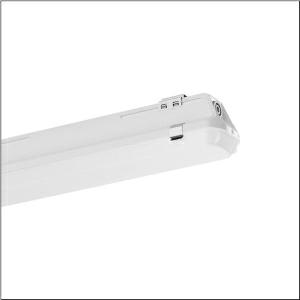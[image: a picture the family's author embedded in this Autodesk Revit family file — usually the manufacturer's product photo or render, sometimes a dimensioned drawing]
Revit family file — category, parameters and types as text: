
# Revit family: monsun_r__11_emergency_51fp107p437h3g_44d6
name_source: partatom
category: Lighting Fixtures
units: mm (PartAtom-declared; Revit-internal decimal feet)

## family parameters
Cut with Voids When Loaded = No
Host = Face
Light Source = No
Part Type = Normal
Room Calculation Point = No
Round Connector Dimension = Use Diameter
Shared = No

## types (1)
- Monsun® 11 emergency (1 x LED, 3840 lm, 24.5 W, 4000K)
    Apparent Load = 25 VA
    CIE Flux Codes = 47 77 93 94 100
    Color Rendering = 80
    Color Temperature = 4000K
    Default Elevation = 1800 mm
    Description = Monsun® 11 emergency, damp-proof luminaire, chain hanger, primary optical cover: enclosure, of PMMA, light emission: direct distribution, primary light characteristic: symmetric, installation type: suspended mounting, surface-mounted, horizontal mounting, vertical mounting, LED, rated luminous flux: 3.840lm, luminous efficacy: 157lm/W, light colour: 840, colour temperature: 4000K, control gear: ECG, with terminal, 4-pole, max. 2.5mm², mains connection: 220..240V, AC, 50/60Hz, rated input power: 25W, control gear: single battery element, battery: NiCd, 4,5Ah, mains connection: 230V, 50Hz, luminaire housing, of glass-fibre reinforced polyester, uncoated, bright grey, incl. chain hanger, length: 1.590mm, width: 90mm, height: 88mm, clip for enclosure, of stainless steel (V2A), ceiling mounting element, of stainless steel (V2A), chain hanger, of stainless steel (V2A), protection rating (complete): IP66, insulation class (complete): insulation class I (protective earthing), certification: CE, UKCA, protection symbol: D, impact resistance: IK04, permissible operating ambient temperature: +5..+35°C, standard: EN 50419, EN 60598-2-1, EN 60598-2-22, no direct snow, no direct sun, no direct rain, for indoor or canopied outdoor use, corresponds to IFS (International Featured Standards) requirements for safety and quality in the food industry, contact your sales advisor before using the luminaires in applications with unclear chemical exposure, large temperature fluctuations or condensation-forming humidity, LABS conformity tested according to VDMA 24364:2018-05, packaging unit: 1 piece
    Height = 89 mm
    Lamp = 1 x LED
    Lamp Light Flux = 3840 lm
    Lamp Power = 24.5 W
    Lamp count = 1
    Length = 1590 mm
    Luminous efficacy = 157 lm/W
    Manufacturer = Siteco
    ModVariant = No
    Model = 51FP107P437H3G
    Mounting Place = Ceiling
    Mounting Type = Surface mounted
    Number of Poles = 1
    OnlyDefault = Yes
    Power Factor = 1
    Product Name = Monsun® 11 emergency
    Product group = damp-proof luminaire
    ProductGroupID = 300
    Protection Class = Protection class I
    Protection Degree = IP 66
    RLX_Detail_Level = 1
    RLX_Emergency_Light_Flux = 0 lm
    RLX_Emergency_Type = 0
    RLX_Emergency_Type_DB = No
    RlxData = <blob elided: 89029 chars, md5=02066452>
    Socket = socket
    Standby Power = 0 W
    System Light Flux = 3840 lm
    System Power = 25 W
    Type Comments = Product without accessories
    Type Image = l_1319650.jpg
    URL = http://relux.com
    VarID = ---
    Voltage = 0 V
    Weight = 0.00 kg
    Width = 90 mm

## geometry (parser evidence)
native form markers: Blend x4, Sweep x13
no freeform markers — native parametric forms only
